# Revit family: HC_Heat Pump_MEPcontent_Itho Daalderop_Amber 65-120_NL-NL1
name_source: partatom
category: Mechanical Equipment
units: mm (PartAtom-declared; Revit-internal decimal feet)

## family parameters
Always vertical = Yes
Classification = None
Cut with Voids When Loaded = No
OmniClass Number = 23.75.10.21
OmniClass Title = Heat Pumps
Part Type = Normal
Room Calculation Point = No
Round Connector Dimension = Use Diameter
Shared = No
Work Plane-Based = No

## types (3) — shared parameters
Article Description = Lucht/water monoblock warmtepomp
Base Family Version = 23.10
Black = Color RGB 040-040-040
Content Supplier URL = www.MEPcontent.com
Custom = No
Dark Gray = Color RGB 050-050-050
Depth = 454 mm  [stored 1.4895 ft]
Description = Lucht/water monoblock warmtepomp
EMCS Version = 5.0
ETIM Article Class = EC011794
Family Version = 23.10
GLN = 8712922000014
Hertz = 50 Hz
Hydronic Return Diameter = 25.4 mm  [stored 0.0833333 ft]
Hydronic Supply Diameter = 25.4 mm  [stored 0.0833333 ft]
IFCExportAs = IfcPump
IFCExportType = NOTDEFINED
Light Gray = Color RAL 7040
MEPcontent Class = HEATPUMP
Manufacturer = Itho Daalderop
Manufacturer URL = https://www.ithodaalderop.nl
Phase = 1
Product Line = Itho Daalderop
Red = Color RGB 255-062-077
Revit Version = 2021
Total Depth = 610 mm  [stored 2.00131 ft]
Total Width = 1320 mm
URL = https://mep.trimble.com
Use Nominal Diameter = Yes
Voltage = 230 V
Width = 1255 mm  [stored 4.11745 ft]
zero-valued in all types: Default Elevation

## per-type parameters (varying)
| type | Fan Offset | GTIN | HR Offset X | HR Offset Y | HS Offset X | HS Offset Y | Height | Main Box Height | Manufacturer Art. No. | Type 120 | Types 65-95 |
| Amber 65 | 470 mm | 8713418050186 | 163.2 mm  [stored 0.535433 ft] | 141.3 mm  [stored 0.463583 ft] | 130.9 mm  [stored 0.429462 ft] | 236.7 mm  [stored 0.776575 ft] | 882 mm  [stored 2.8937 ft] | 824 mm  [stored 2.70341 ft] | 03-00763 | No | Yes |
| Amber 95 | 470 mm | 8713418050193 | 163.2 mm  [stored 0.535433 ft] | 141.3 mm  [stored 0.463583 ft] | 130.9 mm  [stored 0.429462 ft] | 236.7 mm  [stored 0.776575 ft] | 882 mm  [stored 2.8937 ft] | 824 mm  [stored 2.70341 ft] | 03-00764 | No | Yes |
| Amber 120 | 520 mm  [stored 1.70604 ft] | 8713418050209 | 164 mm  [stored 0.538058 ft] | 136.5 mm  [stored 0.447835 ft] | 132.4 mm  [stored 0.434383 ft] | 232.7 mm  [stored 0.763451 ft] | 980 mm  [stored 3.21522 ft] | 922 mm | 03-00765 | Yes | No |

note: column(s) folded — value = type name in every type: Article Type, Model

note: [stored X ft] marks values corroborated as IEEE doubles in the binary element streams (Revit-internal decimal feet)

## geometry (parser evidence)
native form markers: Sweep x20
no freeform markers — native parametric forms only
